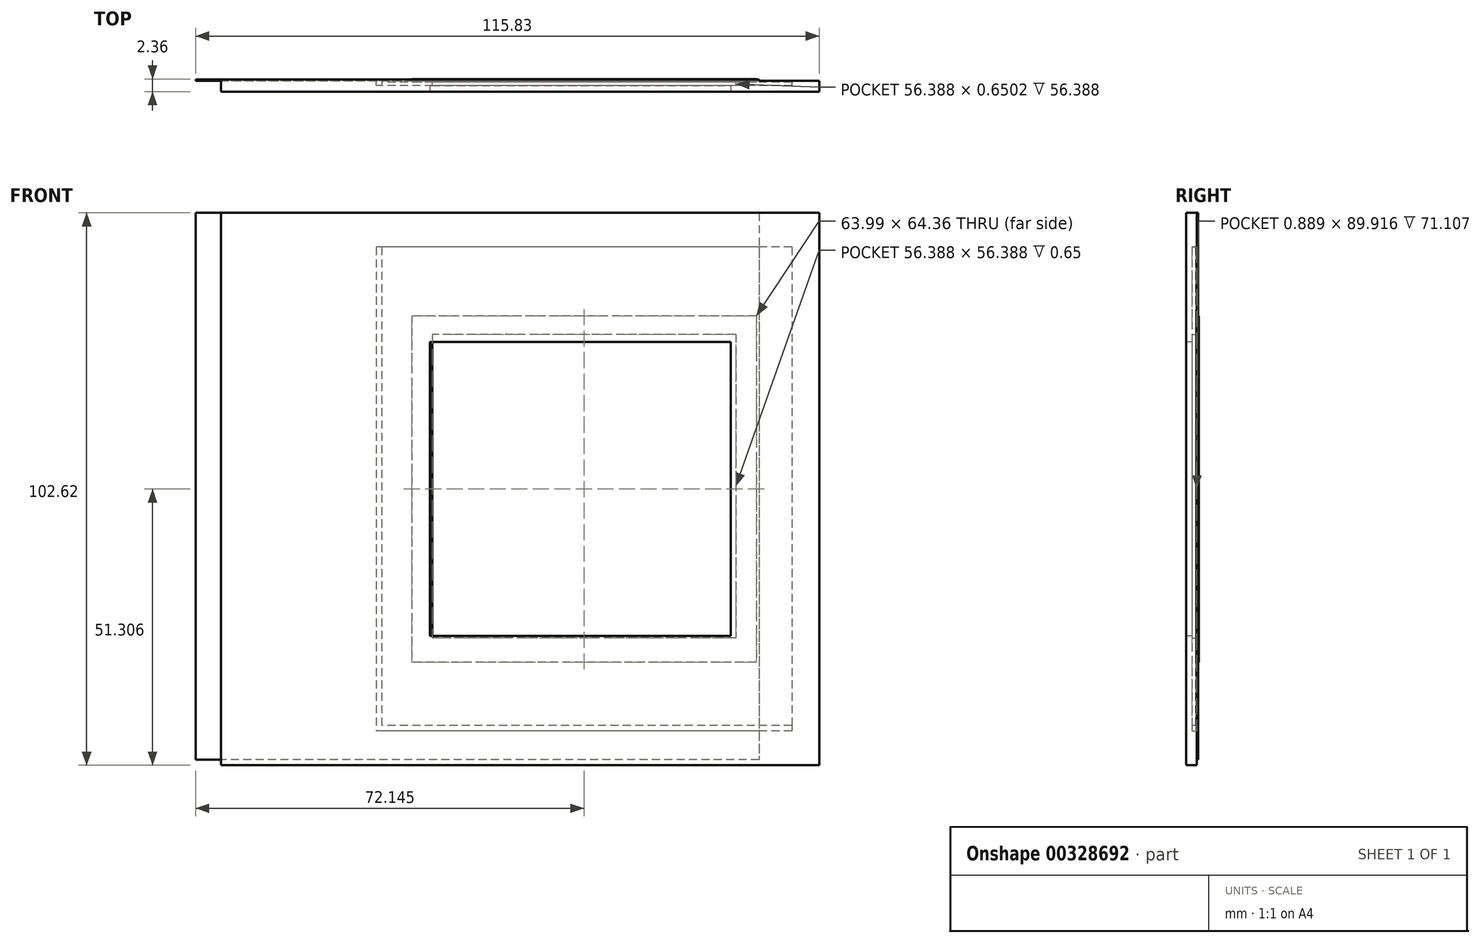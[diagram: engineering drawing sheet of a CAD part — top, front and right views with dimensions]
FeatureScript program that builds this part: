
annotation { "Feature Type Name" : "Feature", "Feature Type Description" : "" }
export const myFeature = defineFeature(function(context is Context, id is Id, definition is map)
    precondition{}
    {
        {
            var Q0;
            Q0=qCreatedBy(makeId("Front.planeOp"),FACE);
            var sketch = newSketch(context, id + "F0", { "sketchPlane" : qUnion([Q0])});
            skLineSegment(sketch, "E0.bottom", {"start": v(-64.46, 46.92) * mm, "end": v(46.66, 46.92) * mm});
            skLineSegment(sketch, "E0.top", {"start": v(-64.46, -55.7) * mm, "end": v(46.66, -55.7) * mm});
            skLineSegment(sketch, "E0.left", {"start": v(-64.46, 46.92) * mm, "end": v(-64.46, -55.7) * mm});
            skLineSegment(sketch, "E0.right", {"start": v(46.66, 46.92) * mm, "end": v(46.66, -55.7) * mm});
            skSolve(sketch);
        }
        {
            var Q0;
            Q0 = qSketchRegion(id + "F0", true);
            extrude(context, id + "F1", {"entities" : qUnion([Q0]), "depth" : 2 * mm});
        }
        {
            var Q0;
            Q0=makeQuery(id+"F1.opExtrude","CAP_FACE",FACE,{"disambiguationData":[OSD([sQuery(id+"F0.wireOp",EDGE,"E0.bottom"),sQuery(id+"F0.wireOp",EDGE,"E0.top"),sQuery(id+"F0.wireOp",EDGE,"E0.left"),sQuery(id+"F0.wireOp",EDGE,"E0.right")])],"isStart":false});
            var sketch = newSketch(context, id + "F2", { "sketchPlane" : qUnion([Q0])});
            skLineSegment(sketch, "E1.bottom", {"start": v(-25.63, 22.91) * mm, "end": v(30.25, 22.91) * mm});
            skLineSegment(sketch, "E1.top", {"start": v(-25.63, -31.7) * mm, "end": v(30.25, -31.7) * mm});
            skLineSegment(sketch, "E1.left", {"start": v(-25.63, 22.91) * mm, "end": v(-25.63, -31.7) * mm});
            skLineSegment(sketch, "E1.right", {"start": v(30.25, 22.91) * mm, "end": v(30.25, -31.7) * mm});
            skSolve(sketch);
        }
        {
            var Q0;
            Q0 = qSketchRegion(id + "F2", true);
            extrude(context, id + "F3", {"entities" : qUnion([Q0]), "operationType" : NewBodyOperationType.REMOVE, "oppositeDirection" : true, "depth" : 1.1 * mm});
        }
        {
            var Q0;
            Q0=makeQuery(id+"F1.opExtrude","CAP_FACE",FACE,{"disambiguationData":[OSD([sQuery(id+"F0.wireOp",EDGE,"E0.bottom"),sQuery(id+"F0.wireOp",EDGE,"E0.top"),sQuery(id+"F0.wireOp",EDGE,"E0.left"),sQuery(id+"F0.wireOp",EDGE,"E0.right")])],"isStart":true});
            var sketch = newSketch(context, id + "F4", { "sketchPlane" : qUnion([Q0])});
            skLineSegment(sketch, "E2.bottom", {"start": v(-41.58, 40.57) * mm, "end": v(35.63, 40.57) * mm});
            skLineSegment(sketch, "E2.top", {"start": v(-41.58, -49.35) * mm, "end": v(35.63, -49.35) * mm});
            skLineSegment(sketch, "E2.left", {"start": v(-41.58, 40.57) * mm, "end": v(-41.58, -49.35) * mm});
            skLineSegment(sketch, "E2.right", {"start": v(35.63, 40.57) * mm, "end": v(35.63, -49.35) * mm});
            skSolve(sketch);
        }
        {
            var Q0;
            Q0 = qSketchRegion(id + "F4", true);
            extrude(context, id + "F5", {"entities" : qUnion([Q0]), "operationType" : NewBodyOperationType.REMOVE, "oppositeDirection" : true, "depth" : 0.89 * mm});
        }
        {
            var Q0;
            Q0=makeQuery(id+"F5.boolean.opBoolean","COPY",FACE,{"derivedFrom":makeQuery(id+"F5.opExtrude","CAP_FACE",FACE,{"disambiguationData":[OSD([sQuery(id+"F4.wireOp",EDGE,"E2.bottom"),sQuery(id+"F4.wireOp",EDGE,"E2.top"),sQuery(id+"F4.wireOp",EDGE,"E2.left"),sQuery(id+"F4.wireOp",EDGE,"E2.right")])],"isStart":false})});
            var sketch = newSketch(context, id + "F6", { "sketchPlane" : qUnion([Q0])});
            skLineSegment(sketch, "E3.bottom", {"start": v(-41.58, 40.57) * mm, "end": v(34.62, 40.57) * mm});
            skLineSegment(sketch, "E3.top", {"start": v(-41.58, -48.33) * mm, "end": v(34.62, -48.33) * mm});
            skLineSegment(sketch, "E3.left", {"start": v(-41.58, 40.57) * mm, "end": v(-41.58, -48.33) * mm});
            skLineSegment(sketch, "E3.right", {"start": v(34.62, 40.57) * mm, "end": v(34.62, -48.33) * mm});
            skSolve(sketch);
        }
        {
            var Q0;
            Q0 = qSketchRegion(id + "F6", true);
            extrude(context, id + "F7", {"entities" : qUnion([Q0]), "operationType" : NewBodyOperationType.ADD, "depth" : 0.65 * mm});
        }
        {
            var Q0;
            Q0=makeQuery(id+"F7.opExtrude","CAP_FACE",FACE,{"disambiguationData":[OSD([sQuery(id+"F6.wireOp",EDGE,"E3.bottom"),sQuery(id+"F6.wireOp",EDGE,"E3.top"),sQuery(id+"F6.wireOp",EDGE,"E3.left"),sQuery(id+"F6.wireOp",EDGE,"E3.right")])],"isStart":false});
            var sketch = newSketch(context, id + "F8", { "sketchPlane" : qUnion([Q0])});
            skLineSegment(sketch, "E4.bottom", {"start": v(-31.17, 24.3) * mm, "end": v(25.22, 24.3) * mm});
            skLineSegment(sketch, "E4.top", {"start": v(-31.17, -32.08) * mm, "end": v(25.22, -32.08) * mm});
            skLineSegment(sketch, "E4.left", {"start": v(-31.17, 24.3) * mm, "end": v(-31.17, -32.08) * mm});
            skLineSegment(sketch, "E4.right", {"start": v(25.22, 24.3) * mm, "end": v(25.22, -32.08) * mm});
            skSolve(sketch);
        }
        {
            var Q0;
            Q0 = qSketchRegion(id + "F8", true);
            extrude(context, id + "F9", {"entities" : qUnion([Q0]), "operationType" : NewBodyOperationType.REMOVE, "oppositeDirection" : true, "depth" : 0.65 * mm});
        }
        {
            var Q0;
            Q0=makeQuery(id+"F7.opExtrude","CAP_FACE",FACE,{"disambiguationData":[OSD([sQuery(id+"F6.wireOp",EDGE,"E3.bottom"),sQuery(id+"F6.wireOp",EDGE,"E3.top"),sQuery(id+"F6.wireOp",EDGE,"E3.left"),sQuery(id+"F6.wireOp",EDGE,"E3.right")])],"isStart":false});
            var sketch = newSketch(context, id + "F10", { "sketchPlane" : qUnion([Q0])});
            skLineSegment(sketch, "E5.bottom", {"start": v(-34.97, 27.79) * mm, "end": v(29.02, 27.79) * mm});
            skLineSegment(sketch, "E5.top", {"start": v(-34.97, -36.57) * mm, "end": v(29.02, -36.57) * mm});
            skLineSegment(sketch, "E5.left", {"start": v(-34.97, 27.79) * mm, "end": v(-34.97, -36.57) * mm});
            skLineSegment(sketch, "E5.right", {"start": v(29.02, 27.79) * mm, "end": v(29.02, -36.57) * mm});
            skSolve(sketch);
        }
        {
            var Q0;
            Q0 = qSketchRegion(id + "F10", true);
            extrude(context, id + "F11", {"entities" : qUnion([Q0]), "operationType" : NewBodyOperationType.ADD, "depth" : 0.6 * mm});
        }
        {
            var Q0;
            Q0=makeQuery(id+"F1.opExtrude","CAP_FACE",FACE,{"disambiguationData":[OSD([sQuery(id+"F0.wireOp",EDGE,"E0.bottom"),sQuery(id+"F0.wireOp",EDGE,"E0.top"),sQuery(id+"F0.wireOp",EDGE,"E0.left"),sQuery(id+"F0.wireOp",EDGE,"E0.right")])],"isStart":true});
            var sketch = newSketch(context, id + "F12", { "sketchPlane" : qUnion([Q0])});
            skLineSegment(sketch, "E6.bottom", {"start": v(-35.47, 46.92) * mm, "end": v(69.17, 46.92) * mm});
            skLineSegment(sketch, "E6.top", {"start": v(-35.47, -54.68) * mm, "end": v(69.17, -54.68) * mm});
            skLineSegment(sketch, "E6.left", {"start": v(-35.47, 46.92) * mm, "end": v(-35.47, -54.68) * mm});
            skLineSegment(sketch, "E6.right", {"start": v(69.17, 46.92) * mm, "end": v(69.17, -54.68) * mm});
            skSolve(sketch);
        }
        {
            var Q0;
            Q0 = qSketchRegion(id + "F12", true);
            extrude(context, id + "F13", {"entities" : qUnion([Q0]), "operationType" : NewBodyOperationType.ADD, "depth" : 0.25 * mm});
        }
    });
